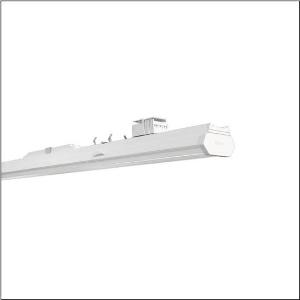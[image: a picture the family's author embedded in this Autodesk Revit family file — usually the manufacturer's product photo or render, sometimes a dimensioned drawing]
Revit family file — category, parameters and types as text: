
# Revit family: licross_11_protected_ho_51tp12dn4fxm3s
name_source: partatom
category: Lighting Fixtures
units: mm (PartAtom-declared; Revit-internal decimal feet)

## family parameters
Cut with Voids When Loaded = No
Host = Face
Light Source = No
Part Type = Normal
Room Calculation Point = No
Round Connector Dimension = Use Diameter
Shared = No

## types (1)
- --- (1 x LED, 970 lm, 7.4 W, 4000K)
    Apparent Load = 7 VA
    CIE Flux Codes = 70 91 97 98 100
    Color Rendering = 80
    Color Temperature = 4000K
    Default Elevation = 1800 mm
    Description = Licross 11 Protected HO, luminaire insert, of sheet steel, galvanised, coil coated, white, length: 1.500mm, width: 90mm, height: 101mm, LED rated luminous flux: 15.270lm, light colour: 840, SDCM (Standard Deviation of Colour Matching)MacAdam ≤ 2 SDCM (initial), control gear: DALI 2 (for two DALI lines), with plug, 6-pole, with phase selection, for trunking rail, 14-core, mains connection: 220..240V, AC, 50/60Hz, rated input power: 91W, for trunking rail, 14-core, internal wiring halogen-free, for emergency light function, converter,control gear: single battery element, battery: LiFePO4, 9Ah, primary light control with lens, of plastic, primary optical cover: cover, of PMMA, light emission: direct distribution, primary light characteristic: symmetric, protection rating (complete): IP64, insulation class (complete): insulation class I (protective earthing), certification: CE, UKCA, protection symbol: D if used in an environment with conductive dust loads with corresponding accessories, impact resistance: IK06, permissible ambient temperature for indoor applications: +5..+30°C, standard: EN 60598-2-22, LABS conformity tested according to VDMA 24364:2018-05, reducing of maximum allowable ambient temperature of 5°C with ceiling mounting, corresponds to IFS (International Featured Standards) requirements for safety and quality in the food industry, The light source and the operating device comply with the requirements of the Ecodesign Regulation (EU) 2019/2020 and are replaceable in accordance with this regulation, packaging unit: 1 piece
    Height = 92 mm
    Lamp = 1 x LED
    Lamp Light Flux = 970 lm
    Lamp Power = 7.4 W
    Lamp count = 1
    Length = 1500 mm
    Luminous efficacy = 131 lm/W
    Manufacturer = Siteco
    ModVariant = No
    Model = 51TP12DN4FXM3S
    Mounting Place = Ceiling
    Mounting Type = Pendant
    Number of Poles = 1
    OnlyDefault = Yes
    Power Factor = 1
    Product Name = Licross 11 Protected HO
    Product group = luminaire insert | ceiling pendant
    ProductGroupID = 901
    Protection Class = Protection class I
    Protection Degree = IP 64
    RLX_Detail_Level = 1
    RLX_Emergency_Light_Flux = 0 lm
    RLX_Emergency_Type = 0
    RLX_Emergency_Type_DB = No
    RlxData = <blob elided: 25125 chars, md5=ea25c281>
    Socket = socket
    Standby Power = 0 W
    System Light Flux = 970 lm
    System Power = 7 W
    Type Comments = : emergency light operation: 3 h
    Type Image = l_1256148.jpg
    URL = http://relux.com
    VarID = @adj_096431
    Voltage = 0 V
    Weight = 0.00 kg
    Width = 88 mm

## geometry (parser evidence)
native form markers: Blend x4, Sweep x11
no freeform markers — native parametric forms only
